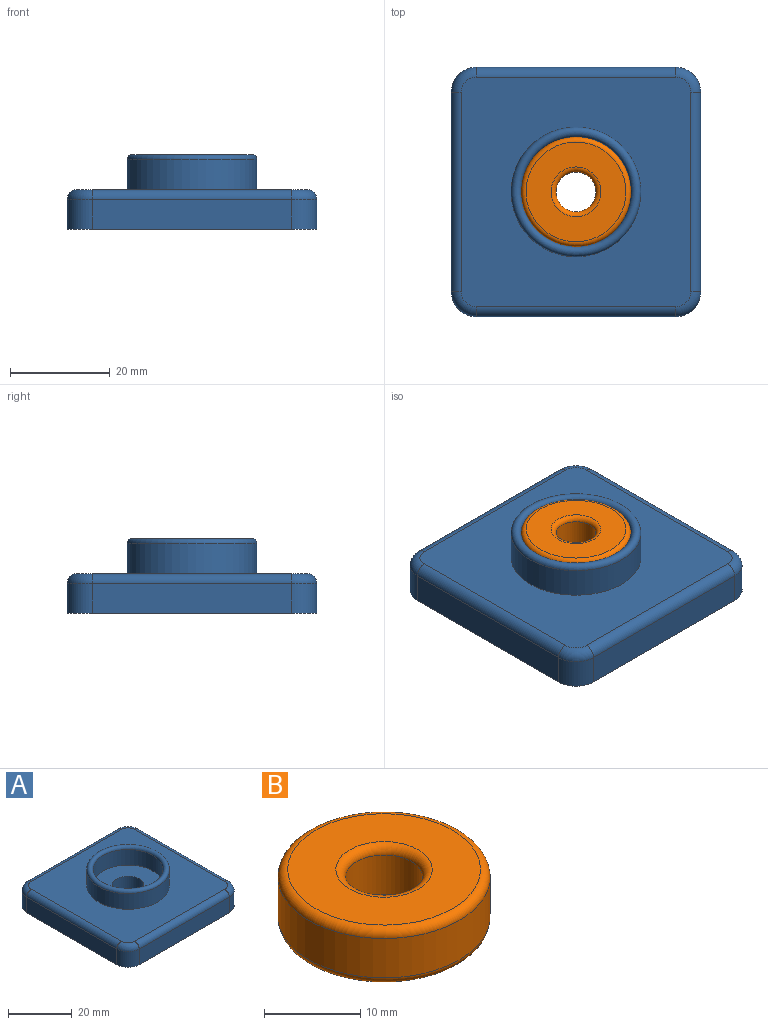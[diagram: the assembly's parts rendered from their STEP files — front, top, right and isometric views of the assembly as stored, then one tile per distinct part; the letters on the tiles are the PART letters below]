
ASSEMBLY  parts=2 mates=1
PART A: 23 faces, bbox 50.8x50.8x15 mm
  f0: plane 46x46mm, normal (0,0,1), area 1577.3mm2, adj f2,f10,f11,f12,f13,f16,f18,f20
  f1: cylinder r=11mm len=22mm, axis (0,0,-1), area 414.7mm2, adj f8,f14
  f2: cylinder r=13mm len=26mm, axis (0,0,-1), area 490.1mm2, adj f0,f14
  f3: plane 50x50mm, normal (0,0,-1), area 2400mm2, adj f4,f5,f6,f7,f9,f15,f17,f19
  f4: plane 40x6mm, normal (1,0,0), area 240mm2, adj f3,f11,f17,f21
  f5: plane 40x6mm, normal (0,1,0), area 240mm2, adj f3,f13,f15,f17
  f6: plane 40x6mm, normal (-1,0,0), area 240mm2, adj f3,f12,f15,f19
  f7: plane 40x6mm, normal (0,-1,0), area 240mm2, adj f3,f10,f19,f21
  f8: plane 22x22mm, normal (0,0,1), area 301.6mm2, adj f1,f9
  f9: cylinder r=5mm len=10mm, axis (0,0,1), area 251.3mm2, adj f3,f8
  f10: cylinder r=2mm len=40mm, axis (-1,0,0), area 125.7mm2, adj f0,f7,f20,f22
  f11: cylinder r=2mm len=40mm, axis (0,-1,0), area 125.7mm2, adj f0,f4,f18,f22
  f12: cylinder r=2mm len=40mm, axis (0,1,0), area 125.7mm2, adj f0,f6,f16,f20
  f13: cylinder r=2mm len=40mm, axis (1,0,0), area 125.7mm2, adj f0,f5,f16,f18
  f14: torus R=12mm, axis (0,0,1), area 236.9mm2, adj f1,f2
  f15: cylinder r=5mm len=6mm, axis (0,0,-1), area 47.1mm2, adj f3,f5,f6,f16
  f16: torus R=3mm, axis (0,0,1), area 21.1mm2, adj f0,f12,f13,f15
  f17: cylinder r=5mm len=6mm, axis (0,0,1), area 47.1mm2, adj f3,f4,f5,f18
  f18: torus R=3mm, axis (0,0,1), area 21.1mm2, adj f0,f11,f13,f17
  f19: cylinder r=5mm len=6mm, axis (0,0,1), area 47.1mm2, adj f3,f6,f7,f20
  f20: torus R=3mm, axis (0,0,1), area 21.1mm2, adj f0,f10,f12,f19
  f21: cylinder r=5mm len=6mm, axis (0,0,-1), area 47.1mm2, adj f3,f4,f7,f22
  f22: torus R=3mm, axis (0,0,1), area 21.1mm2, adj f0,f10,f11,f21
PART B: 8 faces, bbox 23.8x23.8x7 mm
  f0: cylinder r=4mm len=8mm, axis (0,0,-1), area 125.7mm2, adj f4,f6
  f1: cylinder r=11mm len=22mm, axis (0,0,-1), area 345.6mm2, adj f5,f7
  f2: plane 20x20mm, normal (0,0,1), area 235.6mm2, adj f6,f7
  f3: plane 20x20mm, normal (0,0,-1), area 235.6mm2, adj f4,f5
  f4: torus R=5mm, axis (0,0,1), area 43.1mm2, adj f0,f3
  f5: torus R=10mm, axis (0,0,1), area 105mm2, adj f1,f3
  f6: torus R=5mm, axis (0,0,1), area 43.1mm2, adj f0,f2
  f7: torus R=10mm, axis (0,0,1), area 105mm2, adj f1,f2
PLACE A t=(-17.32,-4.27,-1.9)mm
PLACE B rot(axis=(1,0,0),180deg) t=(-17.32,-4.27,13.1)mm
MATE fastened B.f1 <-> A.f2  axis (0,0,-1) through (-17.32,-4.27,6.1)mm
